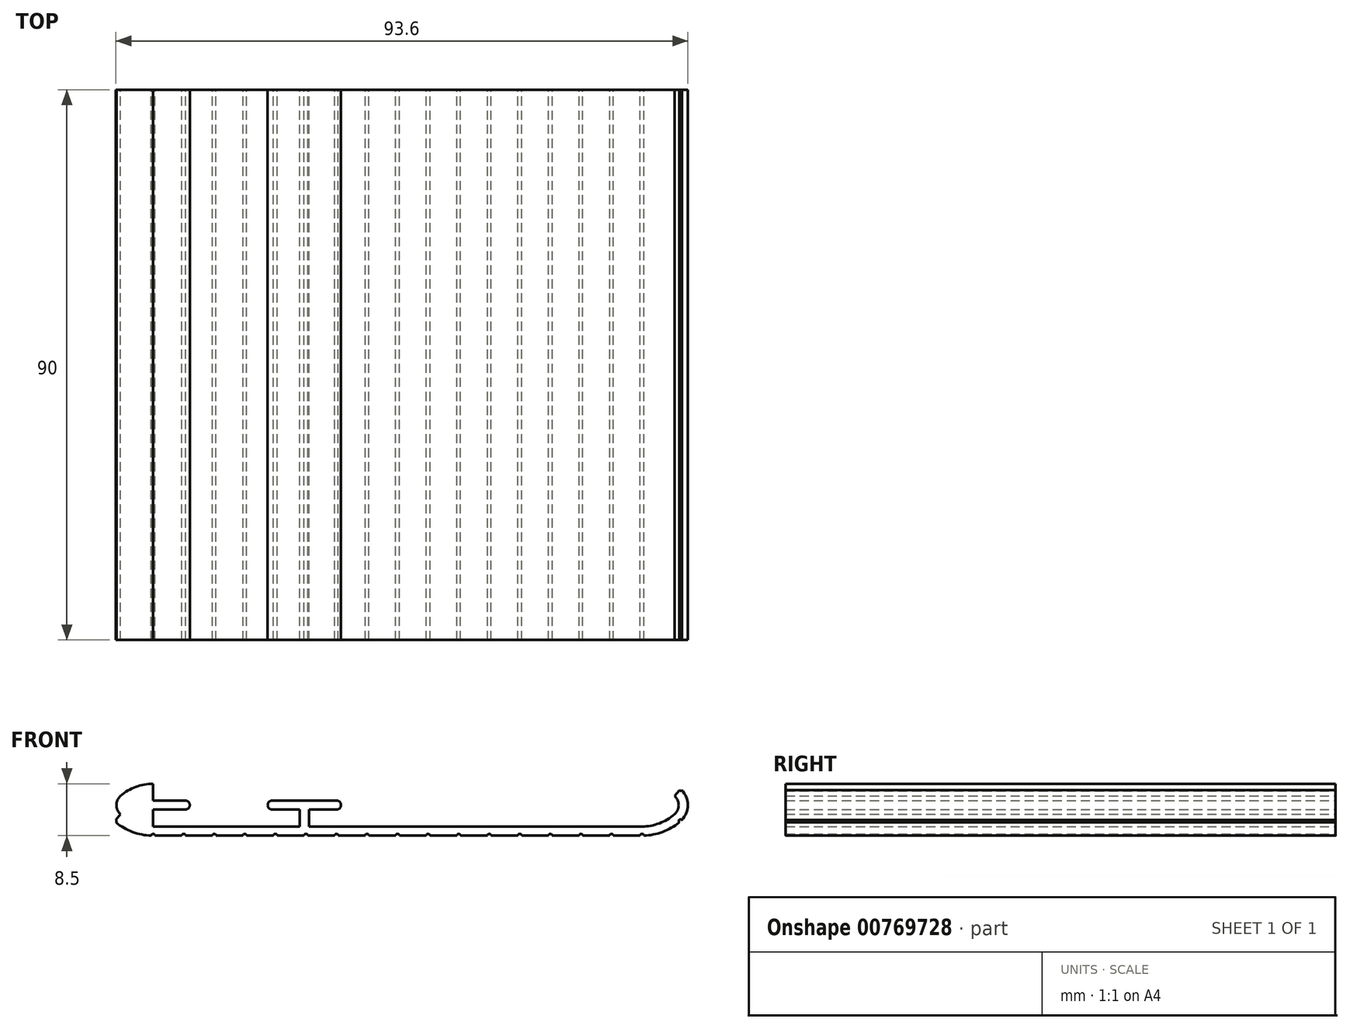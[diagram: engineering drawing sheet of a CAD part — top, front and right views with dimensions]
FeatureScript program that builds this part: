
annotation { "Feature Type Name" : "Feature", "Feature Type Description" : "" }
export const myFeature = defineFeature(function(context is Context, id is Id, definition is map)
    precondition{}
    {
        {
            var Q0;
            Q0=qCreatedBy(makeId("Front.planeOp"),FACE);
            var sketch = newSketch(context, id + "F0", { "sketchPlane" : qUnion([Q0])});
            skLineSegment(sketch, "E0", {"start": v(-47.5, 0) * mm, "end": v(47.5, 0) * mm, "construction": true});
            skLineSegment(sketch, "E1", {"start": v(0, 5) * mm, "end": v(0, -5) * mm, "construction": true});
            skLineSegment(sketch, "E2", {"start": v(0, 5) * mm, "end": v(40, 5) * mm});
            skArc(sketch, "E3", {"start": v(47.5, 0) * mm, "mid": v(47.19, 1.45) * mm, "end": v(46.3, 2.64) * mm});
            skArc(sketch, "E4", {"start": v(40, 5) * mm, "mid": v(43.36, 4.39) * mm, "end": v(46.3, 2.64) * mm});
            skLineSegment(sketch, "E5.MirrorCS", {"start": v(0, 5) * mm, "end": v(-40, 5) * mm});
            skArc(sketch, "E6.MirrorCS", {"start": v(-40, 5) * mm, "mid": v(-43.36, 4.39) * mm, "end": v(-46.3, 2.64) * mm});
            skArc(sketch, "E7.MirrorCS", {"start": v(-47.5, 0) * mm, "mid": v(-47.19, 1.45) * mm, "end": v(-46.3, 2.64) * mm});
            skLineSegment(sketch, "E8.MirrorCS", {"start": v(0, -5) * mm, "end": v(-40, -5) * mm});
            skLineSegment(sketch, "E9.MirrorCS", {"start": v(0, -5) * mm, "end": v(40, -5) * mm});
            skArc(sketch, "E10.MirrorCS", {"start": v(40, -5) * mm, "mid": v(43.36, -4.39) * mm, "end": v(46.3, -2.64) * mm});
            skArc(sketch, "E11.MirrorCS", {"start": v(47.5, 0) * mm, "mid": v(47.19, -1.45) * mm, "end": v(46.3, -2.64) * mm});
            skArc(sketch, "E12.MirrorCS", {"start": v(-40, -5) * mm, "mid": v(-43.36, -4.39) * mm, "end": v(-46.3, -2.64) * mm});
            skArc(sketch, "E13.MirrorCS", {"start": v(-47.5, 0) * mm, "mid": v(-47.19, -1.45) * mm, "end": v(-46.3, -2.64) * mm});
            skSolve(sketch);
        }
        {
            var Q0;
            Q0 = qSketchRegion(id + "F0", true);
            extrude(context, id + "F1", {"entities" : qUnion([Q0]), "depth" : 90 * mm, "offsetDistance" : 25 * mm});
        }
        {
            var Q0;
            Q0=makeQuery(id+"F1.opExtrude","CAP_FACE",FACE,{"disambiguationData":[OSD([sQuery(id+"F0.wireOp",EDGE,"E2"),sQuery(id+"F0.wireOp",EDGE,"E3"),sQuery(id+"F0.wireOp",EDGE,"E4"),sQuery(id+"F0.wireOp",EDGE,"E5.MirrorCS"),sQuery(id+"F0.wireOp",EDGE,"E6.MirrorCS"),sQuery(id+"F0.wireOp",EDGE,"E7.MirrorCS"),sQuery(id+"F0.wireOp",EDGE,"E8.MirrorCS"),sQuery(id+"F0.wireOp",EDGE,"E9.MirrorCS"),sQuery(id+"F0.wireOp",EDGE,"E10.MirrorCS"),sQuery(id+"F0.wireOp",EDGE,"E11.MirrorCS"),sQuery(id+"F0.wireOp",EDGE,"E12.MirrorCS"),sQuery(id+"F0.wireOp",EDGE,"E13.MirrorCS")])],"isStart":false});
            var Q1;
            Q1=makeQuery(id+"F1.opExtrude","CAP_FACE",FACE,{"disambiguationData":[OSD([sQuery(id+"F0.wireOp",EDGE,"E2"),sQuery(id+"F0.wireOp",EDGE,"E3"),sQuery(id+"F0.wireOp",EDGE,"E4"),sQuery(id+"F0.wireOp",EDGE,"E5.MirrorCS"),sQuery(id+"F0.wireOp",EDGE,"E6.MirrorCS"),sQuery(id+"F0.wireOp",EDGE,"E7.MirrorCS"),sQuery(id+"F0.wireOp",EDGE,"E8.MirrorCS"),sQuery(id+"F0.wireOp",EDGE,"E9.MirrorCS"),sQuery(id+"F0.wireOp",EDGE,"E10.MirrorCS"),sQuery(id+"F0.wireOp",EDGE,"E11.MirrorCS"),sQuery(id+"F0.wireOp",EDGE,"E12.MirrorCS"),sQuery(id+"F0.wireOp",EDGE,"E13.MirrorCS")])],"isStart":true});
            shell(context, id + "F2", {"entities" : qUnion([Q0, Q1]), "thickness" : 1.5 * mm});
        }
        {
            var Q0;
            Q0=qCreatedBy(makeId("Front.planeOp"),FACE);
            var sketch = newSketch(context, id + "F3", { "sketchPlane" : qUnion([Q0])});
            skArc(sketch, "E14.0", {"start": v(45.32, 1.5) * mm, "mid": v(46, 0) * mm, "end": v(45.32, -1.5) * mm, "construction": true});
            skArc(sketch, "E15.0", {"start": v(-45.32, -1.5) * mm, "mid": v(-46, 0) * mm, "end": v(-45.32, 1.5) * mm, "construction": true});
            skLineSegment(sketch, "E16", {"start": v(44, 0) * mm, "end": v(52.73, 10) * mm});
            skLineSegment(sketch, "E17", {"start": v(-44, 0) * mm, "end": v(-47.5, -4.01) * mm});
            skLineSegment(sketch, "E18", {"start": v(-47.5, -4.01) * mm, "end": v(-47.5, 10) * mm});
            skLineSegment(sketch, "E19", {"start": v(-47.5, 10) * mm, "end": v(52.73, 10) * mm});
            skLineSegment(sketch, "E20", {"start": v(44, 0) * mm, "end": v(-44, 0) * mm});
            skSolve(sketch);
        }
        {
            var Q0;
            Q0 = qSketchRegion(id + "F3", true);
            extrude(context, id + "F4", {"entities" : qUnion([Q0]), "operationType" : NewBodyOperationType.REMOVE, "endBound" : BoundingType.THROUGH_ALL, "depth" : 25 * mm, "offsetDistance" : 25 * mm});
        }
        {
            var Q0;
            Q0=qCreatedBy(makeId("Front.planeOp"),FACE);
            var sketch = newSketch(context, id + "F5", { "sketchPlane" : qUnion([Q0])});
            skArc(sketch, "E21", {"start": v(-45.32, 1.5) * mm, "mid": v(-46, 0) * mm, "end": v(-45.32, -1.5) * mm});
            skArc(sketch, "E22.0", {"start": v(-40, -3.5) * mm, "mid": v(-42.84, -2.99) * mm, "end": v(-45.32, -1.5) * mm});
            skArc(sketch, "E23.MirrorCS", {"start": v(-40, 3.5) * mm, "mid": v(-42.84, 2.99) * mm, "end": v(-45.32, 1.5) * mm});
            skLineSegment(sketch, "E24", {"start": v(-40, 3.5) * mm, "end": v(-40, 0.75) * mm});
            skPoint(sketch, "E25.orphan", {"position": v(-40, 3.5) * mm});
            skLineSegment(sketch, "E26.trimOffspring", {"start": v(-40, -0.75) * mm, "end": v(-40, -3.5) * mm});
            skLineSegment(sketch, "E27.bottom", {"start": v(-40, 0.75) * mm, "end": v(-34, 0.75) * mm});
            skLineSegment(sketch, "E27.top", {"start": v(-40, -0.75) * mm, "end": v(-34, -0.75) * mm});
            skLineSegment(sketch, "E27.right", {"start": v(-34, 0.75) * mm, "end": v(-34, -0.75) * mm});
            skSolve(sketch);
        }
        {
            var Q0;
            Q0 = qSketchRegion(id + "F5", true);
            var Q1;
            Q1=makeQuery(id+"F1.opExtrude","CAP_FACE",FACE,{"disambiguationData":[OSD([sQuery(id+"F0.wireOp",EDGE,"E2"),sQuery(id+"F0.wireOp",EDGE,"E3"),sQuery(id+"F0.wireOp",EDGE,"E4"),sQuery(id+"F0.wireOp",EDGE,"E5.MirrorCS"),sQuery(id+"F0.wireOp",EDGE,"E6.MirrorCS"),sQuery(id+"F0.wireOp",EDGE,"E7.MirrorCS"),sQuery(id+"F0.wireOp",EDGE,"E8.MirrorCS"),sQuery(id+"F0.wireOp",EDGE,"E9.MirrorCS"),sQuery(id+"F0.wireOp",EDGE,"E10.MirrorCS"),sQuery(id+"F0.wireOp",EDGE,"E11.MirrorCS"),sQuery(id+"F0.wireOp",EDGE,"E12.MirrorCS"),sQuery(id+"F0.wireOp",EDGE,"E13.MirrorCS")])],"isStart":false});
            extrude(context, id + "F6", {"entities" : qUnion([Q0]), "operationType" : NewBodyOperationType.ADD, "endBound" : BoundingType.UP_TO_SURFACE, "depth" : 25 * mm, "endBoundEntityFace" : qUnion([Q1]), "offsetDistance" : 25 * mm});
        }
        {
            var Q0;
            Q0=qCreatedBy(makeId("Front.planeOp"),FACE);
            var sketch = newSketch(context, id + "F7", { "sketchPlane" : qUnion([Q0])});
            skLineSegment(sketch, "E28.top", {"start": v(-16, -3.5) * mm, "end": v(-14.5, -3.5) * mm});
            skLineSegment(sketch, "E28.left", {"start": v(-16, -0.75) * mm, "end": v(-16, -3.5) * mm});
            skLineSegment(sketch, "E28.right", {"start": v(-14.5, -0.75) * mm, "end": v(-14.5, -3.5) * mm});
            skLineSegment(sketch, "E29.bottom", {"start": v(-21.25, 0.75) * mm, "end": v(-9.25, 0.75) * mm});
            skLineSegment(sketch, "E29.top", {"start": v(-21.25, -0.75) * mm, "end": v(-16, -0.75) * mm});
            skLineSegment(sketch, "E29.left", {"start": v(-21.25, 0.75) * mm, "end": v(-21.25, -0.75) * mm});
            skLineSegment(sketch, "E29.right", {"start": v(-9.25, 0.75) * mm, "end": v(-9.25, -0.75) * mm});
            skLineSegment(sketch, "E30.trimOffspring", {"start": v(-14.5, -0.75) * mm, "end": v(-9.25, -0.75) * mm});
            skPoint(sketch, "E31", {"position": v(-21.25, 0) * mm});
            skSolve(sketch);
        }
        {
            var Q0;
            Q0 = qSketchRegion(id + "F7", true);
            var Q1;
            Q1=makeQuery(id+"F6.boolean.opBoolean","MERGE",FACE,{"derivedFrom":[makeQuery(id+"F1.opExtrude","CAP_FACE",FACE,{"disambiguationData":[OSD([sQuery(id+"F0.wireOp",EDGE,"E2"),sQuery(id+"F0.wireOp",EDGE,"E3"),sQuery(id+"F0.wireOp",EDGE,"E4"),sQuery(id+"F0.wireOp",EDGE,"E5.MirrorCS"),sQuery(id+"F0.wireOp",EDGE,"E6.MirrorCS"),sQuery(id+"F0.wireOp",EDGE,"E7.MirrorCS"),sQuery(id+"F0.wireOp",EDGE,"E8.MirrorCS"),sQuery(id+"F0.wireOp",EDGE,"E9.MirrorCS"),sQuery(id+"F0.wireOp",EDGE,"E10.MirrorCS"),sQuery(id+"F0.wireOp",EDGE,"E11.MirrorCS"),sQuery(id+"F0.wireOp",EDGE,"E12.MirrorCS"),sQuery(id+"F0.wireOp",EDGE,"E13.MirrorCS")])],"isStart":false}),makeQuery(id+"F6.opExtrude","CAP_FACE",FACE,{"disambiguationData":[OSD([sQuery(id+"F5.wireOp",EDGE,"E21"),sQuery(id+"F5.wireOp",EDGE,"E22.0"),sQuery(id+"F5.wireOp",EDGE,"E23.MirrorCS"),sQuery(id+"F5.wireOp",EDGE,"E24"),sQuery(id+"F5.wireOp",EDGE,"E26.trimOffspring"),sQuery(id+"F5.wireOp",EDGE,"E27.bottom"),sQuery(id+"F5.wireOp",EDGE,"E27.top"),sQuery(id+"F5.wireOp",EDGE,"E27.right")])],"isStart":false})]});
            extrude(context, id + "F8", {"entities" : qUnion([Q0]), "operationType" : NewBodyOperationType.ADD, "endBound" : BoundingType.UP_TO_SURFACE, "depth" : 25 * mm, "endBoundEntityFace" : qUnion([Q1]), "offsetDistance" : 25 * mm});
        }
        {
            var Q0;
            Q0=makeQuery(id+"F6.opExtrude","SWEPT_EDGE",EDGE,{"disambiguationData":[OSD([sQuery(id+"F5.wireOp",EDGE,"E27.bottom"),sQuery(id+"F5.wireOp",EDGE,"E27.right")])]});
            var Q1;
            Q1=makeQuery(id+"F6.opExtrude","SWEPT_EDGE",EDGE,{"disambiguationData":[OSD([sQuery(id+"F5.wireOp",EDGE,"E27.top"),sQuery(id+"F5.wireOp",EDGE,"E27.right")])]});
            var Q2;
            Q2=makeQuery(id+"F8.opExtrude","SWEPT_EDGE",EDGE,{"disambiguationData":[OSD([sQuery(id+"F7.wireOp",EDGE,"E29.bottom"),sQuery(id+"F7.wireOp",EDGE,"E29.right")])]});
            var Q3;
            Q3=makeQuery(id+"F8.opExtrude","SWEPT_EDGE",EDGE,{"disambiguationData":[OSD([sQuery(id+"F7.wireOp",EDGE,"E29.right"),sQuery(id+"F7.wireOp",EDGE,"E30.trimOffspring")])]});
            var Q4;
            Q4=makeQuery(id+"F8.opExtrude","SWEPT_EDGE",EDGE,{"disambiguationData":[OSD([sQuery(id+"F7.wireOp",EDGE,"E29.bottom"),sQuery(id+"F7.wireOp",EDGE,"E29.left")])]});
            var Q5;
            Q5=makeQuery(id+"F8.opExtrude","SWEPT_EDGE",EDGE,{"disambiguationData":[OSD([sQuery(id+"F7.wireOp",EDGE,"E29.top"),sQuery(id+"F7.wireOp",EDGE,"E29.left")])]});
            fillet(context, id + "F9", {"entities" : qUnion([Q0, Q1, Q2, Q3, Q4, Q5]), "radius" : .75 * mm, "tangentPropagation" : true, "allowEdgeOverflow" : false});
        }
        {
            var Q0;
            Q0=qCreatedBy(makeId("Front.planeOp"),FACE);
            var sketch = newSketch(context, id + "F10", { "sketchPlane" : qUnion([Q0])});
            skCircle(sketch, "E32", {"center": v(40, -5) * mm, "radius": 0.3 * mm});
            skCircle(sketch, "E33.1.0.0", {"center": v(35, -5) * mm, "radius": 0.3 * mm});
            skCircle(sketch, "E33.2.0.0", {"center": v(30, -5) * mm, "radius": 0.3 * mm});
            skLineSegment(sketch, "E33.direction1", {"start": v(35, -5) * mm, "end": v(40, -5) * mm, "construction": true});
            skCircle(sketch, "E34.0.3.0", {"center": v(25, -5) * mm, "radius": 0.3 * mm});
            skCircle(sketch, "E34.0.4.0", {"center": v(20, -5) * mm, "radius": 0.3 * mm});
            skCircle(sketch, "E34.0.5.0", {"center": v(15, -5) * mm, "radius": 0.3 * mm});
            skCircle(sketch, "E34.0.6.0", {"center": v(10, -5) * mm, "radius": 0.3 * mm});
            skCircle(sketch, "E34.0.7.0", {"center": v(5, -5) * mm, "radius": 0.3 * mm});
            skCircle(sketch, "E34.0.8.0", {"center": v(0, -5) * mm, "radius": 0.3 * mm});
            skCircle(sketch, "E35", {"center": v(46.3, -2.64) * mm, "radius": 0.3 * mm});
            skCircle(sketch, "E36.0.9.0", {"center": v(-5, -5) * mm, "radius": 0.3 * mm});
            skCircle(sketch, "E36.0.10.0", {"center": v(-10, -5) * mm, "radius": 0.3 * mm});
            skCircle(sketch, "E36.0.11.0", {"center": v(-15, -5) * mm, "radius": 0.3 * mm});
            skCircle(sketch, "E36.0.12.0", {"center": v(-20, -5) * mm, "radius": 0.3 * mm});
            skCircle(sketch, "E36.0.13.0", {"center": v(-25, -5) * mm, "radius": 0.3 * mm});
            skCircle(sketch, "E36.0.14.0", {"center": v(-30, -5) * mm, "radius": 0.3 * mm});
            skCircle(sketch, "E36.0.15.0", {"center": v(-35, -5) * mm, "radius": 0.3 * mm});
            skCircle(sketch, "E36.0.16.0", {"center": v(-40, -5) * mm, "radius": 0.3 * mm});
            skCircle(sketch, "E37", {"center": v(46.3, 2.64) * mm, "radius": 0.3 * mm});
            skCircle(sketch, "E38", {"center": v(-46.3, -2.64) * mm, "radius": 0.3 * mm});
            skSolve(sketch);
        }
        {
            var Q0;
            Q0 = qSketchRegion(id + "F10", true);
            extrude(context, id + "F11", {"entities" : qUnion([Q0]), "operationType" : NewBodyOperationType.REMOVE, "endBound" : BoundingType.THROUGH_ALL, "depth" : 25 * mm, "offsetDistance" : 25 * mm});
        }
    });
